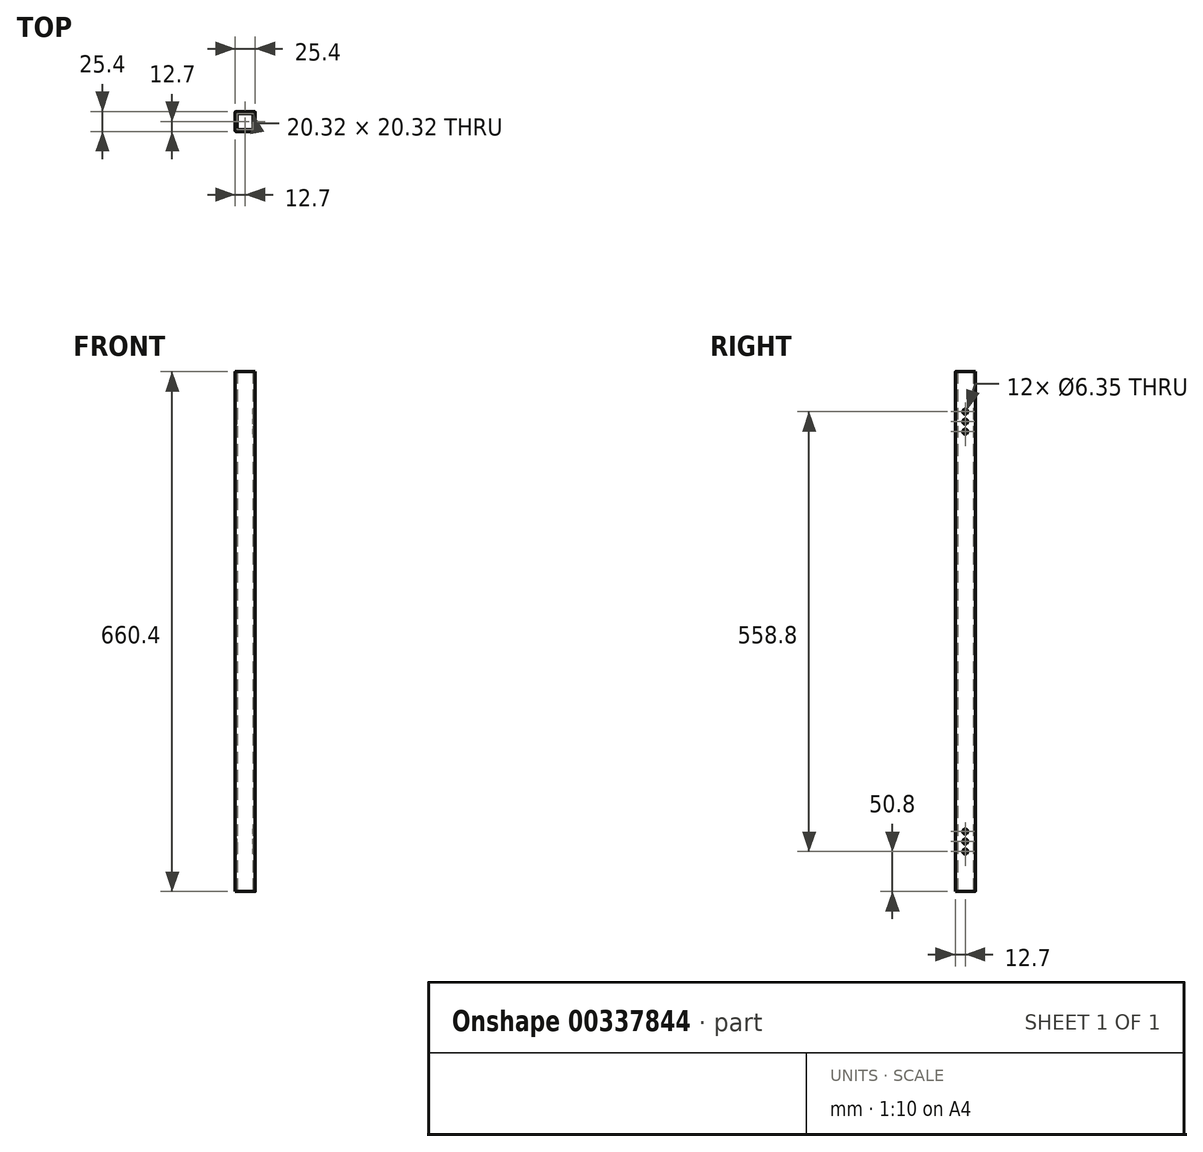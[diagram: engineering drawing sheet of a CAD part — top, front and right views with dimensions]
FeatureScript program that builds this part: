
annotation { "Feature Type Name" : "Feature", "Feature Type Description" : "" }
export const myFeature = defineFeature(function(context is Context, id is Id, definition is map)
    precondition{}
    {
        {
            var Q0;
            Q0=qCreatedBy(makeId("Top.planeOp"),FACE);
            var sketch = newSketch(context, id + "F0", { "sketchPlane" : qUnion([Q0])});
            skPoint(sketch, "E0", {"position": v(0, 0) * mm});
            skPoint(sketch, "E1", {"position": v(12.7, 0) * mm});
            skPoint(sketch, "E2", {"position": v(12.7, 12.7) * mm});
            skLineSegment(sketch, "E3.bottom", {"start": v(12.7, 12.7) * mm, "end": v(-12.7, 12.7) * mm});
            skLineSegment(sketch, "E3.top", {"start": v(12.7, -12.7) * mm, "end": v(-12.7, -12.7) * mm});
            skLineSegment(sketch, "E3.left", {"start": v(12.7, 12.7) * mm, "end": v(12.7, -12.7) * mm});
            skLineSegment(sketch, "E3.right", {"start": v(-12.7, 12.7) * mm, "end": v(-12.7, -12.7) * mm});
            skLineSegment(sketch, "E4.0", {"start": v(10.16, 10.16) * mm, "end": v(-10.16, 10.16) * mm});
            skLineSegment(sketch, "E5.0", {"start": v(10.16, 10.16) * mm, "end": v(10.16, -10.16) * mm});
            skLineSegment(sketch, "E6.0", {"start": v(10.16, -10.16) * mm, "end": v(-10.16, -10.16) * mm});
            skLineSegment(sketch, "E7.0", {"start": v(-10.16, 10.16) * mm, "end": v(-10.16, -10.16) * mm});
            skSolve(sketch);
        }
        {
            var Q0;
            Q0=makeQuery(id+"F0.imprint","IMPRINT",FACE,{"disambiguationData":[TD([[makeQuery(id+"F0.imprint","IMPRINT",EDGE,{"derivedFrom":sQuery(id+"F0.wireOp",EDGE,"E3.bottom")}),1.0]])]});
            extrude(context, id + "F1", {"entities" : qUnion([Q0]), "depth" : 660.4 * mm});
        }
        {
            var Q0;
            Q0=qCreatedBy(makeId("Right.planeOp"),FACE);
            cPlane(context, id + "F2", {"entities" : qUnion([Q0]), "cplaneType" : CPlaneType.OFFSET, "offset" : 12.7 * mm, "width" : 152.4 * mm, "height" : 152.4 * mm});
        }
        {
            var Q0;
            Q0=qCreatedBy(id+"F2.planeOp",FACE);
            var sketch = newSketch(context, id + "F3", { "sketchPlane" : qUnion([Q0])});
            skPoint(sketch, "E8", {"position": v(0, 0) * mm});
            skPoint(sketch, "E9", {"position": v(0, 50.8) * mm});
            skPoint(sketch, "E10", {"position": v(0, 63.5) * mm});
            skPoint(sketch, "E11", {"position": v(0, 76.2) * mm});
            skPoint(sketch, "E12", {"position": v(0, 660.4) * mm});
            skPoint(sketch, "E13", {"position": v(0, 609.6) * mm});
            skPoint(sketch, "E14", {"position": v(0, 596.9) * mm});
            skPoint(sketch, "E15", {"position": v(0, 584.2) * mm});
            skSolve(sketch);
        }
        {
            var Q0;
            Q0=sQuery(id+"F3.wireOp",VERTEX,"E13");
            var Q1;
            Q1=sQuery(id+"F3.wireOp",VERTEX,"E14");
            var Q2;
            Q2=sQuery(id+"F3.wireOp",VERTEX,"E15");
            var Q3;
            Q3=sQuery(id+"F3.wireOp",VERTEX,"E11");
            var Q4;
            Q4=sQuery(id+"F3.wireOp",VERTEX,"E10");
            var Q5;
            Q5=sQuery(id+"F3.wireOp",VERTEX,"E9");
            var Q6;
            Q6=makeQuery(id+"F1.opExtrude","SWEPT_BODY",BODY,{"disambiguationData":[OSD([sQuery(id+"F0.wireOp",EDGE,"E3.bottom"),sQuery(id+"F0.wireOp",EDGE,"E3.top"),sQuery(id+"F0.wireOp",EDGE,"E3.left"),sQuery(id+"F0.wireOp",EDGE,"E3.right"),sQuery(id+"F0.wireOp",EDGE,"E4.0"),sQuery(id+"F0.wireOp",EDGE,"E5.0"),sQuery(id+"F0.wireOp",EDGE,"E6.0"),sQuery(id+"F0.wireOp",EDGE,"E7.0")])]});
            hole(context, id + "F4", {"style" : HoleStyle.SIMPLE, "endStyle" : HoleEndStyle.THROUGH, "holeDiameter" : 6.35 * mm, "tappedDepth" : 12.7 * mm, "tapClearance" : 3, "locations" : qUnion([Q0, Q1, Q2, Q3, Q4, Q5]), "scope" : qUnion([Q6])});
        }
        {
            var Q0;
            Q0=makeQuery(id+"F1.opExtrude","SWEPT_EDGE",EDGE,{"disambiguationData":[OSD([sQuery(id+"F0.wireOp",EDGE,"E3.bottom"),sQuery(id+"F0.wireOp",EDGE,"E3.left")])]});
            var Q1;
            Q1=makeQuery(id+"F1.opExtrude","SWEPT_EDGE",EDGE,{"disambiguationData":[OSD([sQuery(id+"F0.wireOp",EDGE,"E3.bottom"),sQuery(id+"F0.wireOp",EDGE,"E3.right")])]});
            var Q2;
            Q2=makeQuery(id+"F1.opExtrude","SWEPT_EDGE",EDGE,{"disambiguationData":[OSD([sQuery(id+"F0.wireOp",EDGE,"E3.top"),sQuery(id+"F0.wireOp",EDGE,"E3.left")])]});
            var Q3;
            Q3=makeQuery(id+"F1.opExtrude","SWEPT_EDGE",EDGE,{"disambiguationData":[OSD([sQuery(id+"F0.wireOp",EDGE,"E3.top"),sQuery(id+"F0.wireOp",EDGE,"E3.right")])]});
            fillet(context, id + "F5", {"entities" : qUnion([Q0, Q1, Q2, Q3]), "radius" : 0.76 * mm, "tangentPropagation" : true, "allowEdgeOverflow" : false});
        }
    });
